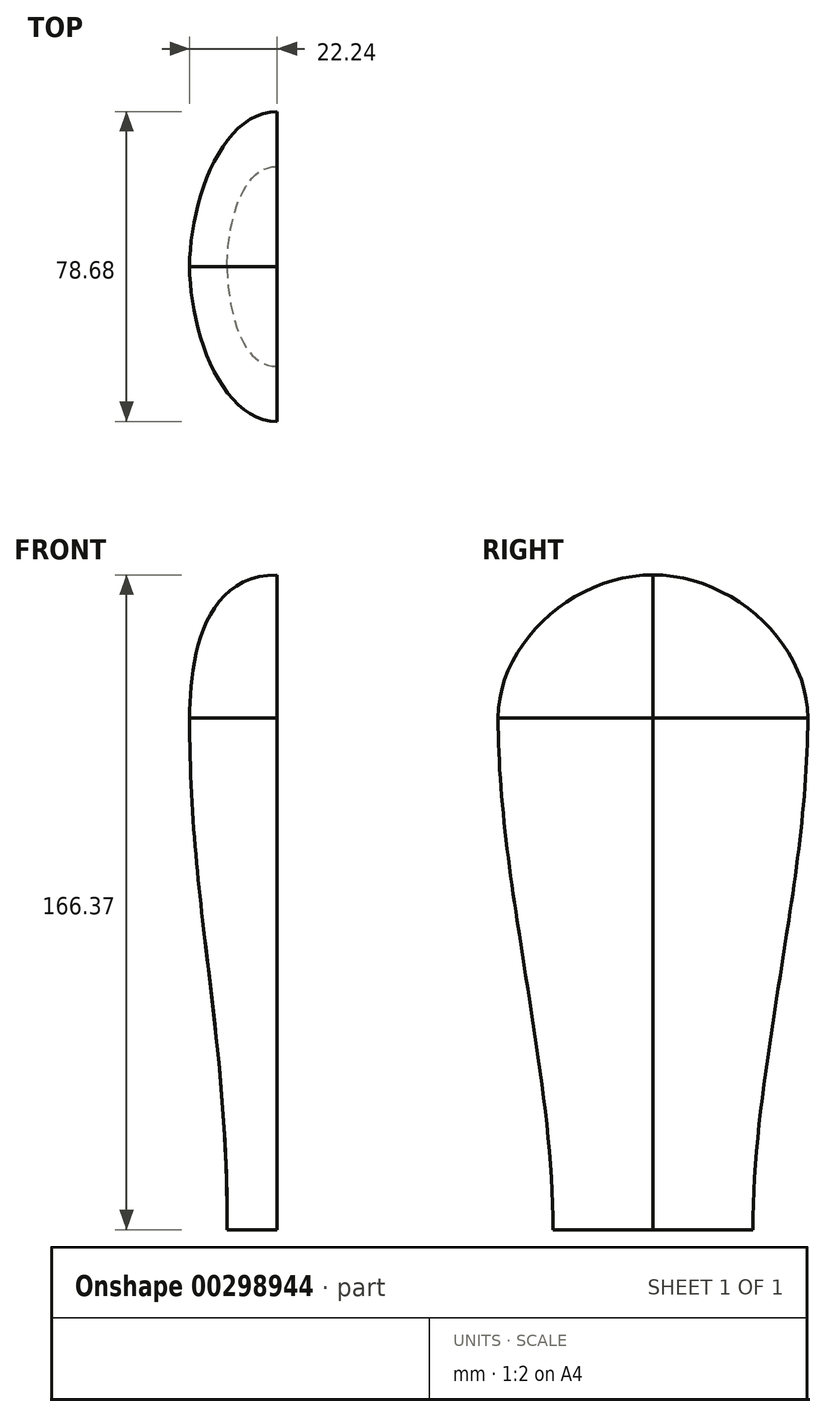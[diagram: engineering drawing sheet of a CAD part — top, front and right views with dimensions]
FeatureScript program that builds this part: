
annotation { "Feature Type Name" : "Feature", "Feature Type Description" : "" }
export const myFeature = defineFeature(function(context is Context, id is Id, definition is map)
    precondition{}
    {
        {
            var Q0;
            Q0=qCreatedBy(makeId("Front.planeOp"),FACE);
            var sketch = newSketch(context, id + "F0", { "sketchPlane" : qUnion([Q0])});
            skFitSpline(sketch, "E0", {"points": [v(0, 36.35) * mm, v(-22.24, 0) * mm], "startDerivative": vector(-57.7, 0) * mm, "endDerivative": vector(0, -42.62) * mm});
            skLineSegment(sketch, "E1", {"start": v(-22.24, 0) * mm, "end": v(-22.24, -15.6) * mm, "construction": true});
            skLineSegment(sketch, "E2", {"start": v(0, 36.35) * mm, "end": v(12.95, 36.35) * mm, "construction": true});
            skSolve(sketch);
        }
        {
            var Q0;
            Q0=qCreatedBy(makeId("Right.planeOp"),FACE);
            var sketch = newSketch(context, id + "F1", { "sketchPlane" : qUnion([Q0])});
            skFitSpline(sketch, "E3", {"points": [v(0, 36.35) * mm, v(-39.34, 0) * mm], "startDerivative": vector(-59.43, 0) * mm, "endDerivative": vector(0, -57.78) * mm});
            skLineSegment(sketch, "E4", {"start": v(0, 36.35) * mm, "end": v(13.28, 36.35) * mm, "construction": true});
            skLineSegment(sketch, "E5", {"start": v(-39.34, 0) * mm, "end": v(-39.34, -16.27) * mm, "construction": true});
            skSolve(sketch);
        }
        {
            var Q0;
            Q0=qCreatedBy(makeId("Top.planeOp"),FACE);
            var sketch = newSketch(context, id + "F2", { "sketchPlane" : qUnion([Q0])});
            skFitSpline(sketch, "E6", {"points": [v(-22.24, 0) * mm, v(0, -39.34) * mm], "startDerivative": vector(0, -47.71) * mm, "endDerivative": vector(43.11, 0) * mm});
            skLineSegment(sketch, "E7", {"start": v(-22.24, 0) * mm, "end": v(-22.24, 18.17) * mm, "construction": true});
            skLineSegment(sketch, "E8", {"start": v(0, -39.34) * mm, "end": v(16.44, -39.34) * mm, "construction": true});
            skSolve(sketch);
        }
        {
            var Q0;
            Q0=sQuery(id+"F0.wireOp",EDGE,"E0");
            var Q1;
            Q1=sQuery(id+"F1.wireOp",EDGE,"E3");
            var Q2;
            Q2=sQuery(id+"F2.wireOp",EDGE,"E6");
            loft(context, id + "F3", {"bodyType" : ToolBodyType.SURFACE, "addGuides" : true, "wireProfilesArray" : [{ "wireProfileEntities" : qUnion([Q0]) }, { "wireProfileEntities" : qUnion([Q1]) }], "guidesArray" : [{ "guideEntities" : qUnion([Q2]), "guideDerivativeType" : LoftGuideDerivativeType.DEFAULT, "guideDerivativeMagnitude" : 1 }]});
        }
        {
            var Q0;
            Q0=qCreatedBy(makeId("Right.planeOp"),FACE);
            var sketch = newSketch(context, id + "F4", { "sketchPlane" : qUnion([Q0])});
            skFitSpline(sketch, "E9", {"points": [v(-39.34, 0) * mm, v(-25.4, -130.02) * mm], "startDerivative": vector(0, -125.75) * mm, "endDerivative": vector(0, -124.42) * mm});
            skLineSegment(sketch, "E10", {"start": v(-25.4, -130.02) * mm, "end": v(0, -130.02) * mm, "construction": true});
            skLineSegment(sketch, "E11", {"start": v(-25.4, -130.02) * mm, "end": v(-25.4, -167.73) * mm, "construction": true});
            skSolve(sketch);
        }
        {
            var Q0;
            Q0=qCreatedBy(makeId("Top.planeOp"),FACE);
            var Q1;
            Q1=sQuery(id+"F4.wireOp",VERTEX,"E11.start");
            cPlane(context, id + "F5", {"entities" : qUnion([Q0, Q1]), "cplaneType" : CPlaneType.PLANE_POINT, "offset" : 68.58 * mm, "oppositeDirection" : true, "width" : 152.4 * mm, "height" : 152.4 * mm});
        }
        {
            var Q0;
            Q0=qCreatedBy(id+"F5.planeOp",FACE);
            var sketch = newSketch(context, id + "F6", { "sketchPlane" : qUnion([Q0])});
            skFitSpline(sketch, "E12", {"points": [v(-12.7, 0) * mm, v(0, -25.4) * mm], "startDerivative": vector(0, -26.97) * mm, "endDerivative": vector(29.63, 0) * mm});
            skLineSegment(sketch, "E13", {"start": v(-12.7, 0) * mm, "end": v(-12.7, 11.12) * mm, "construction": true});
            skLineSegment(sketch, "E14", {"start": v(0, -25.4) * mm, "end": v(22.85, -25.4) * mm, "construction": true});
            skSolve(sketch);
        }
        {
            var Q0;
            Q0=qCreatedBy(makeId("Front.planeOp"),FACE);
            var sketch = newSketch(context, id + "F7", { "sketchPlane" : qUnion([Q0])});
            skFitSpline(sketch, "E15", {"points": [v(-22.24, 0) * mm, v(-12.7, -130.02) * mm], "startDerivative": vector(0, -146.32) * mm, "endDerivative": vector(0, -155.68) * mm});
            skLineSegment(sketch, "E16", {"start": v(-12.7, -130.02) * mm, "end": v(-12.7, -156.64) * mm, "construction": true});
            skSolve(sketch);
        }
        {
            var Q0;
            Q0=sQuery(id+"F7.wireOp",EDGE,"E15");
            var Q1;
            Q1=sQuery(id+"F4.wireOp",EDGE,"E9");
            var Q2;
            Q2=makeQuery(id+"F3.opLoft","SWEPT_EDGE",EDGE,{"disambiguationData":[OSD([sQuery(id+"F2.wireOp",EDGE,"E6")])]});
            var Q3;
            Q3=sQuery(id+"F6.wireOp",EDGE,"E12");
            loft(context, id + "F8", {"bodyType" : ToolBodyType.SURFACE, "addGuides" : true, "wireProfilesArray" : [{ "wireProfileEntities" : qUnion([Q0]) }, { "wireProfileEntities" : qUnion([Q1]) }], "guidesArray" : [{ "guideEntities" : qUnion([Q2]), "guideDerivativeType" : LoftGuideDerivativeType.DEFAULT, "guideDerivativeMagnitude" : 1 }, { "guideEntities" : qUnion([Q3]), "guideDerivativeType" : LoftGuideDerivativeType.DEFAULT, "guideDerivativeMagnitude" : 1 }]});
        }
        {
            var Q0;
            Q0=makeQuery(id+"F8.opLoft","SWEPT_BODY",BODY,{"disambiguationData":[OSD([sQuery(id+"F2.wireOp",EDGE,"E6"),sQuery(id+"F4.wireOp",EDGE,"E9"),sQuery(id+"F6.wireOp",EDGE,"E12"),sQuery(id+"F7.wireOp",EDGE,"E15")])]});
            var Q1;
            Q1=makeQuery(id+"F3.opLoft","SWEPT_BODY",BODY,{"disambiguationData":[OSD([sQuery(id+"F0.wireOp",EDGE,"E0"),sQuery(id+"F1.wireOp",EDGE,"E3"),sQuery(id+"F2.wireOp",EDGE,"E6")])]});
            var Q2;
            Q2=qCreatedBy(makeId("Front.planeOp"),FACE);
            mirror(context, id + "F9", {"entities" : qUnion([Q0, Q1]), "mirrorPlane" : qUnion([Q2])});
        }
    });
